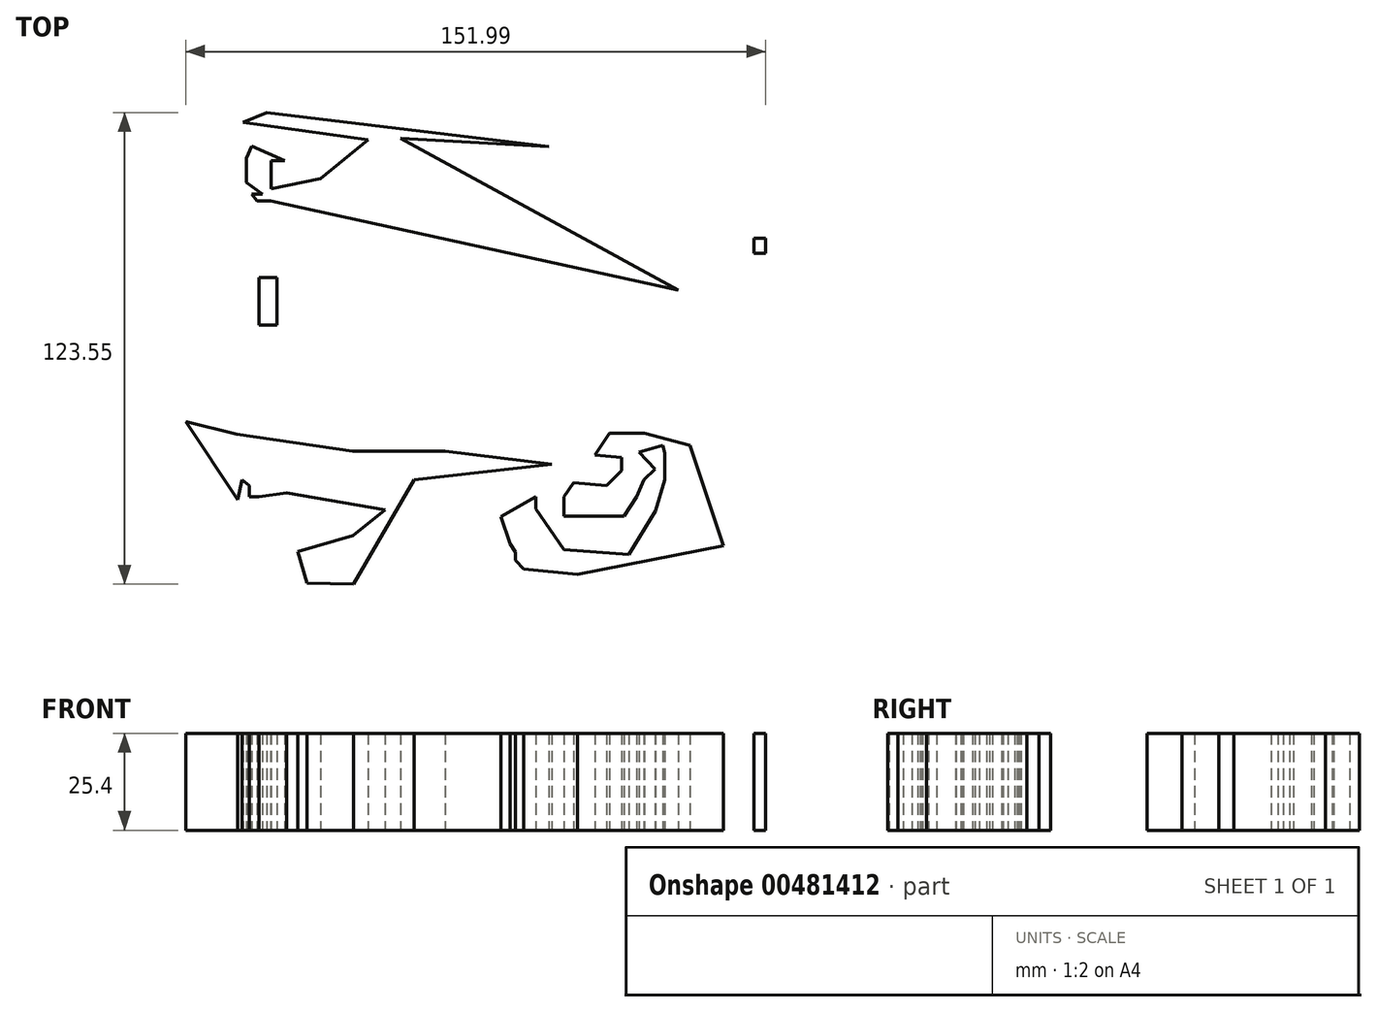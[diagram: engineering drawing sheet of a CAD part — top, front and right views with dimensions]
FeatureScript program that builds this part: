
annotation { "Feature Type Name" : "Feature", "Feature Type Description" : "" }
export const myFeature = defineFeature(function(context is Context, id is Id, definition is map)
    precondition{}
    {
        {
            var Q0;
            Q0=qCreatedBy(makeId("Top.planeOp"),FACE);
            var sketch = newSketch(context, id + "F0", { "sketchPlane" : qUnion([Q0])});
            skLineSegment(sketch, "E0.bottom", {"start": v(-75.8, 75.93) * mm, "end": v(76.2, 75.93) * mm});
            skLineSegment(sketch, "E0.top", {"start": v(-75.8, -76.2) * mm, "end": v(76.2, -76.2) * mm});
            skLineSegment(sketch, "E0.left", {"start": v(-75.8, 75.93) * mm, "end": v(-75.8, -76.2) * mm});
            skLineSegment(sketch, "E0.right", {"start": v(76.2, 75.93) * mm, "end": v(76.2, -76.2) * mm});
            skLineSegment(sketch, "E1.bottom", {"start": v(-75.8, 75.93) * mm, "end": v(-3.13, 75.93) * mm});
            skLineSegment(sketch, "E1.top", {"start": v(-75.8, 27.08) * mm, "end": v(-3.13, 27.08) * mm});
            skLineSegment(sketch, "E1.left", {"start": v(-75.8, 75.93) * mm, "end": v(-75.8, 27.08) * mm});
            skLineSegment(sketch, "E1.right", {"start": v(-3.13, 75.93) * mm, "end": v(-3.13, 27.08) * mm});
            skLineSegment(sketch, "E2", {"start": v(-3.13, 27.08) * mm, "end": v(76.2, 27.08) * mm});
            skLineSegment(sketch, "E3", {"start": v(76.2, 36.74) * mm, "end": v(73.07, 36.74) * mm});
            skLineSegment(sketch, "E4", {"start": v(73.07, 36.74) * mm, "end": v(73.07, 40.69) * mm});
            skLineSegment(sketch, "E5", {"start": v(73.07, 40.69) * mm, "end": v(76.2, 40.69) * mm});
            skLineSegment(sketch, "E6", {"start": v(-56.6, 27.08) * mm, "end": v(-56.6, 30.34) * mm});
            skLineSegment(sketch, "E7", {"start": v(-56.6, 30.34) * mm, "end": v(-51.84, 30.34) * mm});
            skLineSegment(sketch, "E8", {"start": v(-51.84, 30.34) * mm, "end": v(-51.84, 27.08) * mm});
            skLineSegment(sketch, "E9", {"start": v(-51.84, 27.08) * mm, "end": v(-51.84, 17.96) * mm});
            skLineSegment(sketch, "E10", {"start": v(-51.84, 17.96) * mm, "end": v(-56.6, 17.96) * mm});
            skLineSegment(sketch, "E11", {"start": v(-56.6, 17.96) * mm, "end": v(-56.6, 27.08) * mm});
            skLineSegment(sketch, "E12", {"start": v(-8.44, 27.08) * mm, "end": v(-8.44, -7.35) * mm});
            skLineSegment(sketch, "E13", {"start": v(-8.44, -7.35) * mm, "end": v(-75.8, -7.35) * mm});
            skLineSegment(sketch, "E14", {"start": v(-75.8, -7.35) * mm, "end": v(76.2, -7.35) * mm});
            skLineSegment(sketch, "E15", {"start": v(76.2, -7.35) * mm, "end": v(76.2, 27.08) * mm});
            skLineSegment(sketch, "E16", {"start": v(-75.8, -7.35) * mm, "end": v(-62.18, -27.76) * mm});
            skLineSegment(sketch, "E17", {"start": v(-62.18, -27.76) * mm, "end": v(-60.96, -22.59) * mm});
            skLineSegment(sketch, "E18", {"start": v(-60.96, -22.59) * mm, "end": v(-59.06, -24.08) * mm});
            skLineSegment(sketch, "E19", {"start": v(-59.06, -24.08) * mm, "end": v(-59.06, -27.08) * mm});
            skLineSegment(sketch, "E20", {"start": v(-59.06, -27.08) * mm, "end": v(-56.6, -27.08) * mm});
            skLineSegment(sketch, "E21", {"start": v(-56.6, -27.08) * mm, "end": v(-49.4, -25.99) * mm});
            skLineSegment(sketch, "E22", {"start": v(-49.4, -25.99) * mm, "end": v(-23.54, -30.48) * mm});
            skLineSegment(sketch, "E23", {"start": v(-23.54, -30.48) * mm, "end": v(-31.98, -37.15) * mm});
            skLineSegment(sketch, "E24", {"start": v(-31.98, -37.15) * mm, "end": v(-46.4, -41.37) * mm});
            skLineSegment(sketch, "E25", {"start": v(-46.4, -41.37) * mm, "end": v(-43.98, -49.64) * mm});
            skLineSegment(sketch, "E26", {"start": v(-43.98, -49.64) * mm, "end": v(-31.84, -49.94) * mm});
            skLineSegment(sketch, "E27", {"start": v(-31.84, -49.94) * mm, "end": v(-15.92, -22.59) * mm});
            skLineSegment(sketch, "E28", {"start": v(-15.92, -22.59) * mm, "end": v(20.14, -18.5) * mm});
            skLineSegment(sketch, "E29", {"start": v(31.84, -19.6) * mm, "end": v(20.14, -18.5) * mm});
            skLineSegment(sketch, "E30", {"start": v(31.43, -16.06) * mm, "end": v(38.47, -16.71) * mm});
            skLineSegment(sketch, "E31", {"start": v(38.47, -16.71) * mm, "end": v(38.47, -20.14) * mm});
            skLineSegment(sketch, "E32", {"start": v(38.47, -20.14) * mm, "end": v(34.43, -24.08) * mm});
            skLineSegment(sketch, "E33", {"start": v(34.43, -24.08) * mm, "end": v(25.8, -23.28) * mm});
            skLineSegment(sketch, "E34", {"start": v(25.8, -23.28) * mm, "end": v(23.27, -27.08) * mm});
            skLineSegment(sketch, "E35", {"start": v(23.27, -27.08) * mm, "end": v(23.27, -32.11) * mm});
            skLineSegment(sketch, "E36", {"start": v(23.27, -32.11) * mm, "end": v(39.05, -32.11) * mm});
            skLineSegment(sketch, "E37", {"start": v(39.05, -32.11) * mm, "end": v(42.32, -27.08) * mm});
            skLineSegment(sketch, "E38", {"start": v(42.32, -27.08) * mm, "end": v(44.22, -22.59) * mm});
            skLineSegment(sketch, "E39", {"start": v(44.22, -22.59) * mm, "end": v(47.22, -19.73) * mm});
            skLineSegment(sketch, "E40", {"start": v(47.22, -19.73) * mm, "end": v(42.97, -15.28) * mm});
            skLineSegment(sketch, "E41", {"start": v(42.97, -15.28) * mm, "end": v(49.26, -13.6) * mm});
            skLineSegment(sketch, "E42", {"start": v(49.26, -13.6) * mm, "end": v(49.79, -15.59) * mm});
            skLineSegment(sketch, "E43", {"start": v(49.79, -15.59) * mm, "end": v(49.79, -18.5) * mm});
            skLineSegment(sketch, "E44", {"start": v(49.79, -18.5) * mm, "end": v(49.79, -22.59) * mm});
            skLineSegment(sketch, "E45", {"start": v(49.79, -22.59) * mm, "end": v(47.35, -30.75) * mm});
            skLineSegment(sketch, "E46", {"start": v(47.35, -30.75) * mm, "end": v(40.28, -42.18) * mm});
            skLineSegment(sketch, "E47", {"start": v(40.28, -42.18) * mm, "end": v(23.27, -40.82) * mm});
            skLineSegment(sketch, "E48", {"start": v(23.27, -40.82) * mm, "end": v(15.92, -30.2) * mm});
            skLineSegment(sketch, "E49", {"start": v(15.92, -30.2) * mm, "end": v(15.92, -27.08) * mm});
            skLineSegment(sketch, "E50", {"start": v(15.92, -27.08) * mm, "end": v(6.8, -32.25) * mm});
            skLineSegment(sketch, "E51", {"start": v(6.8, -32.25) * mm, "end": v(9.25, -39.32) * mm});
            skLineSegment(sketch, "E52", {"start": v(9.25, -39.32) * mm, "end": v(10.61, -41.5) * mm});
            skLineSegment(sketch, "E53", {"start": v(10.61, -41.5) * mm, "end": v(10.61, -43.68) * mm});
            skLineSegment(sketch, "E54", {"start": v(10.61, -43.68) * mm, "end": v(12.8, -46) * mm});
            skLineSegment(sketch, "E55", {"start": v(12.8, -46) * mm, "end": v(15.6, -46.25) * mm});
            skLineSegment(sketch, "E56", {"start": v(15.6, -46.25) * mm, "end": v(22.92, -46.93) * mm});
            skLineSegment(sketch, "E57", {"start": v(22.92, -46.93) * mm, "end": v(26.84, -47.3) * mm});
            skLineSegment(sketch, "E58", {"start": v(26.84, -47.3) * mm, "end": v(65.04, -39.87) * mm});
            skLineSegment(sketch, "E59", {"start": v(65.04, -39.87) * mm, "end": v(56.33, -13.6) * mm});
            skLineSegment(sketch, "E60", {"start": v(56.33, -13.6) * mm, "end": v(44.36, -10.34) * mm});
            skLineSegment(sketch, "E61", {"start": v(44.36, -10.34) * mm, "end": v(35.24, -10.34) * mm});
            skLineSegment(sketch, "E62", {"start": v(35.24, -10.34) * mm, "end": v(31.43, -16.06) * mm});
            skLineSegment(sketch, "E63", {"start": v(31.84, -19.6) * mm, "end": v(31.43, -16.06) * mm});
            skLineSegment(sketch, "E64", {"start": v(-75.8, -7.35) * mm, "end": v(-62.46, -10.61) * mm});
            skLineSegment(sketch, "E65", {"start": v(-62.46, -10.61) * mm, "end": v(-32.11, -15.1) * mm});
            skLineSegment(sketch, "E66", {"start": v(-32.11, -15.1) * mm, "end": v(-7.76, -15.1) * mm});
            skLineSegment(sketch, "E67", {"start": v(-7.76, -15.1) * mm, "end": v(20.14, -18.5) * mm});
            skSolve(sketch);
        }
        {
            var Q0;
            {var subQ0=sQuery(id+"F0.wireOp",EDGE,"E3");Q0=makeQuery(id+"F0.imprint","IMPRINT",FACE,{"disambiguationData":[TD([[makeQuery(id+"F0.imprint","IMPRINT",EDGE,{"derivedFrom":subQ0}),-1.0]])]});}
            var Q1;
            {var subQ2=sQuery(id+"F0.wireOp",EDGE,"E9");Q1=makeQuery(id+"F0.imprint","IMPRINT",FACE,{"disambiguationData":[TD([[makeQuery(id+"F0.imprint","IMPRINT",EDGE,{"derivedFrom":subQ2}),-1.0]])]});}
            var Q2;
            {var subQ0=sQuery(id+"F0.wireOp",EDGE,"E6");Q2=makeQuery(id+"F0.imprint","IMPRINT",FACE,{"disambiguationData":[TD([[makeQuery(id+"F0.imprint","IMPRINT",EDGE,{"derivedFrom":subQ0}),-1.0]])]});}
            var Q3;
            Q3=makeQuery(id+"F0.imprint","IMPRINT",FACE,{"disambiguationData":[TD([[makeQuery(id+"F0.imprint","IMPRINT",EDGE,{"derivedFrom":sQuery(id+"F0.wireOp",EDGE,"E30")}),1.0]])]});
            var Q4;
            Q4=makeQuery(id+"F0.imprint","IMPRINT",FACE,{"disambiguationData":[TD([[makeQuery(id+"F0.imprint","IMPRINT",EDGE,{"derivedFrom":sQuery(id+"F0.wireOp",EDGE,"E16")}),1.0]])]});
            extrude(context, id + "F1", {"entities" : qUnion([Q0, Q1, Q2, Q3, Q4]), "depth" : 25.4 * mm});
        }
        {
            var Q0;
            Q0=qCreatedBy(makeId("Top.planeOp"),FACE);
            var sketch = newSketch(context, id + "F2", { "sketchPlane" : qUnion([Q0])});
            skLineSegment(sketch, "E68", {"start": v(-60.82, 71.03) * mm, "end": v(-28.03, 66.4) * mm});
            skLineSegment(sketch, "E69", {"start": v(-28.03, 66.4) * mm, "end": v(-40.41, 56.33) * mm});
            skLineSegment(sketch, "E70", {"start": v(-40.41, 56.33) * mm, "end": v(-53.34, 53.61) * mm});
            skLineSegment(sketch, "E71", {"start": v(-53.34, 53.61) * mm, "end": v(-53.34, 60.96) * mm});
            skLineSegment(sketch, "E72", {"start": v(-53.34, 60.96) * mm, "end": v(-49.8, 60.96) * mm});
            skLineSegment(sketch, "E73", {"start": v(-49.8, 60.96) * mm, "end": v(-58.51, 64.77) * mm});
            skLineSegment(sketch, "E74", {"start": v(-58.51, 64.77) * mm, "end": v(-59.88, 61.64) * mm});
            skLineSegment(sketch, "E75", {"start": v(-59.88, 61.64) * mm, "end": v(-59.88, 58.65) * mm});
            skLineSegment(sketch, "E76", {"start": v(-59.88, 58.65) * mm, "end": v(-59.88, 55.25) * mm});
            skLineSegment(sketch, "E77", {"start": v(-58.51, 52.25) * mm, "end": v(-55.65, 52.25) * mm});
            skLineSegment(sketch, "E78", {"start": v(-55.65, 52.25) * mm, "end": v(-59.88, 55.25) * mm});
            skLineSegment(sketch, "E79", {"start": v(-58.51, 52.25) * mm, "end": v(-57.08, 50.48) * mm});
            skPoint(sketch, "E79.endSnap0", {"position": v(-57.08, 52.25) * mm});
            skLineSegment(sketch, "E80", {"start": v(-57.08, 50.48) * mm, "end": v(-54.56, 50.48) * mm});
            skLineSegment(sketch, "E81", {"start": v(-54.56, 50.48) * mm, "end": v(-53.48, 50.48) * mm});
            skLineSegment(sketch, "E82", {"start": v(-53.48, 50.48) * mm, "end": v(53.34, 27.08) * mm});
            skLineSegment(sketch, "E83", {"start": v(53.34, 27.08) * mm, "end": v(-19.46, 66.81) * mm});
            skLineSegment(sketch, "E84", {"start": v(-19.46, 66.81) * mm, "end": v(19.32, 64.63) * mm});
            skLineSegment(sketch, "E85", {"start": v(19.32, 64.63) * mm, "end": v(-54.56, 73.61) * mm});
            skLineSegment(sketch, "E86", {"start": v(-54.56, 73.61) * mm, "end": v(-60.82, 71.03) * mm});
            skSolve(sketch);
        }
        {
            var Q0;
            Q0=makeQuery(id+"F2.imprint","IMPRINT",FACE,{"disambiguationData":[TD([[makeQuery(id+"F2.imprint","IMPRINT",EDGE,{"derivedFrom":sQuery(id+"F2.wireOp",EDGE,"E68")}),1.0]])]});
            extrude(context, id + "F3", {"entities" : qUnion([Q0]), "depth" : 25.4 * mm});
        }
    });
